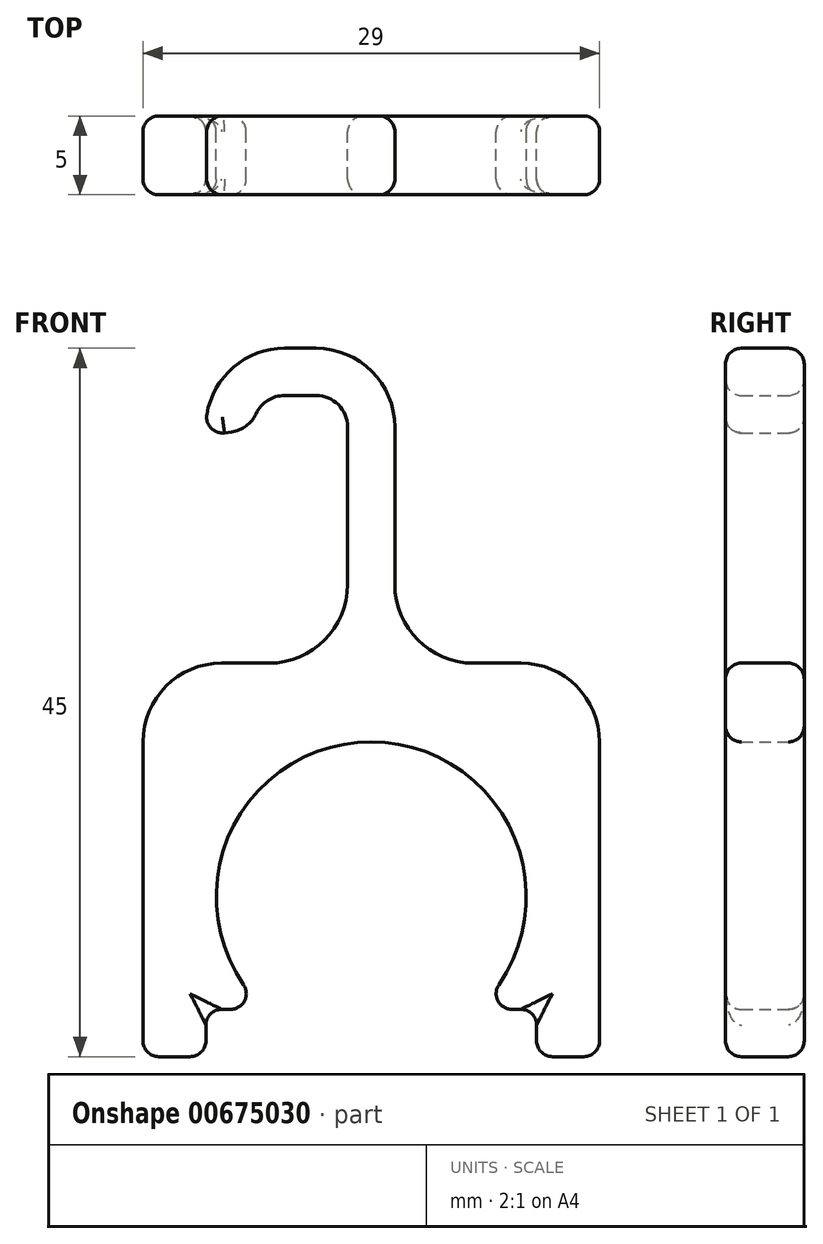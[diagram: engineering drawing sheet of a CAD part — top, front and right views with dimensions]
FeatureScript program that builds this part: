
annotation { "Feature Type Name" : "Feature", "Feature Type Description" : "" }
export const myFeature = defineFeature(function(context is Context, id is Id, definition is map)
    precondition{}
    {
        {
            var Q0;
            Q0=qCreatedBy(makeId("Front.planeOp"),FACE);
            var sketch = newSketch(context, id + "F0", { "sketchPlane" : qUnion([Q0])});
            skArc(sketch, "E0", {"start": v(6.77, -7.15) * mm, "mid": v(0, 9.85) * mm, "end": v(-6.77, -7.15) * mm});
            skLineSegment(sketch, "E1.bottom", {"start": v(-14.5, -7.15) * mm, "end": v(-6.77, -7.15) * mm});
            skLineSegment(sketch, "E2", {"start": v(14.5, -7.15) * mm, "end": v(14.5, 14.85) * mm});
            skLineSegment(sketch, "E3", {"start": v(0, 9.85) * mm, "end": v(0, 14.85) * mm, "construction": true});
            skLineSegment(sketch, "E4", {"start": v(0, 14.85) * mm, "end": v(14.5, 14.85) * mm});
            skLineSegment(sketch, "E5", {"start": v(-14.5, -7.15) * mm, "end": v(-14.5, 14.85) * mm});
            skLineSegment(sketch, "E6", {"start": v(-14.5, 14.85) * mm, "end": v(0, 14.85) * mm});
            skLineSegment(sketch, "E7.trimOffspring", {"start": v(6.77, -7.15) * mm, "end": v(14.5, -7.15) * mm});
            skLineSegment(sketch, "E8", {"start": v(6.77, -7.15) * mm, "end": v(-6.77, -7.15) * mm, "construction": true});
            skLineSegment(sketch, "E9", {"start": v(0, 0) * mm, "end": v(0, -7.15) * mm, "construction": true});
            skLineSegment(sketch, "E10", {"start": v(-1.5, 14.85) * mm, "end": v(-1.5, 29.84) * mm});
            skLineSegment(sketch, "E11", {"start": v(-1.5, 29.84) * mm, "end": v(1.5, 29.84) * mm});
            skLineSegment(sketch, "E12", {"start": v(1.5, 29.84) * mm, "end": v(1.5, 14.85) * mm});
            skArc(sketch, "E13", {"start": v(1.5, 29.84) * mm, "mid": v(0.04, 33.38) * mm, "end": v(-3.5, 34.84) * mm});
            skArc(sketch, "E14", {"start": v(-1.5, 29.84) * mm, "mid": v(-2.09, 31.26) * mm, "end": v(-3.5, 31.84) * mm});
            skLineSegment(sketch, "E15", {"start": v(-14.5, -7.15) * mm, "end": v(-14.5, -10.15) * mm});
            skLineSegment(sketch, "E16", {"start": v(-14.5, -10.15) * mm, "end": v(-10.5, -10.15) * mm});
            skLineSegment(sketch, "E17", {"start": v(-10.5, -10.15) * mm, "end": v(-10.5, -7.15) * mm});
            skLineSegment(sketch, "E18", {"start": v(14.5, -7.15) * mm, "end": v(14.5, -10.15) * mm});
            skLineSegment(sketch, "E19", {"start": v(14.5, -10.15) * mm, "end": v(10.5, -10.15) * mm});
            skLineSegment(sketch, "E20", {"start": v(10.5, -10.15) * mm, "end": v(10.5, -7.15) * mm});
            skLineSegment(sketch, "E21", {"start": v(-3.5, 29.84) * mm, "end": v(-3.5, 34.84) * mm, "construction": true});
            skPoint(sketch, "E22.orphan", {"position": v(-5.5, 29.84) * mm});
            skPoint(sketch, "E23.orphan", {"position": v(-8.5, 29.85) * mm});
            skLineSegment(sketch, "E24", {"start": v(-3.5, 31.84) * mm, "end": v(-5.5, 31.84) * mm});
            skLineSegment(sketch, "E25", {"start": v(-3.5, 34.84) * mm, "end": v(-5.5, 34.84) * mm});
            skArc(sketch, "E26", {"start": v(-5.5, 31.84) * mm, "mid": v(-6.96, 31.22) * mm, "end": v(-7.5, 29.72) * mm});
            skArc(sketch, "E27.0", {"start": v(-5.5, 34.84) * mm, "mid": v(-9.22, 33.19) * mm, "end": v(-10.47, 29.32) * mm});
            skLineSegment(sketch, "E28", {"start": v(-7.5, 29.72) * mm, "end": v(-10.47, 29.32) * mm});
            skSolve(sketch);
        }
        {
            var Q0;
            {var subQ0=sQuery(id+"F0.wireOp",EDGE,"E10");Q0=makeQuery(id+"F0.imprint","IMPRINT",FACE,{"disambiguationData":[TD([[makeQuery(id+"F0.imprint","IMPRINT",EDGE,{"derivedFrom":subQ0}),-1.0]])]});}
            var Q1;
            Q1=makeQuery(id+"F0.imprint","IMPRINT",FACE,{"disambiguationData":[TD([[makeQuery(id+"F0.imprint","IMPRINT",EDGE,{"derivedFrom":sQuery(id+"F0.wireOp",EDGE,"E11")}),1.0]])]});
            var Q2;
            Q2=makeQuery(id+"F0.imprint","IMPRINT",FACE,{"disambiguationData":[TD([[makeQuery(id+"F0.imprint","IMPRINT",EDGE,{"derivedFrom":sQuery(id+"F0.wireOp",EDGE,"E0")}),-1.0]])]});
            var Q3;
            {var subQ0=sQuery(id+"F0.wireOp",EDGE,"E15");Q3=makeQuery(id+"F0.imprint","IMPRINT",FACE,{"disambiguationData":[TD([[makeQuery(id+"F0.imprint","IMPRINT",EDGE,{"derivedFrom":subQ0}),1.0]])]});}
            var Q4;
            {var subQ0=sQuery(id+"F0.wireOp",EDGE,"E18");Q4=makeQuery(id+"F0.imprint","IMPRINT",FACE,{"disambiguationData":[TD([[makeQuery(id+"F0.imprint","IMPRINT",EDGE,{"derivedFrom":subQ0}),-1.0]])]});}
            extrude(context, id + "F1", {"entities" : qUnion([Q0, Q1, Q2, Q3, Q4]), "depth" : 5 * mm, "offsetDistance" : 25 * mm});
        }
        {
            var Q0;
            Q0=makeQuery(id+"F1.opExtrude","SWEPT_EDGE",EDGE,{"disambiguationData":[OSD([sQuery(id+"F0.wireOp",EDGE,"iK1HZVFs-EU1M-R8Xy-Kw5s-u2PyRseDFcwY"),sQuery(id+"F0.wireOp",EDGE,"iyGj0UfU-Zjkc-Cnsw-hSJO-qxqU3gxrafzM")])]});
            var Q1;
            Q1=makeQuery(id+"F1.opExtrude","SWEPT_EDGE",EDGE,{"disambiguationData":[OSD([sQuery(id+"F0.wireOp",EDGE,"E14"),sQuery(id+"F0.wireOp",EDGE,"iyGj0UfU-Zjkc-Cnsw-hSJO-qxqU3gxrafzM")])]});
            var Q2;
            Q2=makeQuery(id+"F1.opExtrude","SWEPT_EDGE",EDGE,{"disambiguationData":[OSD([sQuery(id+"F0.wireOp",EDGE,"E0"),sQuery(id+"F0.wireOp",EDGE,"E1.bottom")])]});
            var Q3;
            Q3=makeQuery(id+"F1.opExtrude","SWEPT_EDGE",EDGE,{"disambiguationData":[OSD([sQuery(id+"F0.wireOp",EDGE,"E0"),sQuery(id+"F0.wireOp",EDGE,"E7.trimOffspring")])]});
            fillet(context, id + "F2", {"entities" : qUnion([Q0, Q1, Q2, Q3]), "radius" : 1 * mm, "tangentPropagation" : true, "allowEdgeOverflow" : false});
        }
        {
            var Q0;
            Q0=makeQuery(id+"F1.opExtrude","SWEPT_EDGE",EDGE,{"disambiguationData":[OSD([sQuery(id+"F0.wireOp",EDGE,"E5"),sQuery(id+"F0.wireOp",EDGE,"E6")])]});
            var Q1;
            Q1=makeQuery(id+"F1.opExtrude","SWEPT_EDGE",EDGE,{"disambiguationData":[OSD([sQuery(id+"F0.wireOp",EDGE,"E6"),sQuery(id+"F0.wireOp",EDGE,"E10")])]});
            var Q2;
            Q2=makeQuery(id+"F1.opExtrude","SWEPT_EDGE",EDGE,{"disambiguationData":[OSD([sQuery(id+"F0.wireOp",EDGE,"E4"),sQuery(id+"F0.wireOp",EDGE,"E12")])]});
            var Q3;
            Q3=makeQuery(id+"F1.opExtrude","SWEPT_EDGE",EDGE,{"disambiguationData":[OSD([sQuery(id+"F0.wireOp",EDGE,"E2"),sQuery(id+"F0.wireOp",EDGE,"E4")])]});
            fillet(context, id + "F3", {"entities" : qUnion([Q0, Q1, Q2, Q3]), "radius" : 5 * mm, "tangentPropagation" : true, "allowEdgeOverflow" : false});
        }
        {
            var Q0;
            Q0=makeQuery(id+"F1.opExtrude","CAP_FACE",FACE,{"disambiguationData":[OSD([sQuery(id+"F0.wireOp",EDGE,"E0"),sQuery(id+"F0.wireOp",EDGE,"E1.bottom"),sQuery(id+"F0.wireOp",EDGE,"E2"),sQuery(id+"F0.wireOp",EDGE,"E4"),sQuery(id+"F0.wireOp",EDGE,"E5"),sQuery(id+"F0.wireOp",EDGE,"E6"),sQuery(id+"F0.wireOp",EDGE,"E7.trimOffspring"),sQuery(id+"F0.wireOp",EDGE,"E10"),sQuery(id+"F0.wireOp",EDGE,"E12"),sQuery(id+"F0.wireOp",EDGE,"E13"),sQuery(id+"F0.wireOp",EDGE,"E14"),sQuery(id+"F0.wireOp",EDGE,"iK1HZVFs-EU1M-R8Xy-Kw5s-u2PyRseDFcwY"),sQuery(id+"F0.wireOp",EDGE,"iyGj0UfU-Zjkc-Cnsw-hSJO-qxqU3gxrafzM")])],"isStart":false});
            var Q1;
            Q1=makeQuery(id+"F1.opExtrude","CAP_FACE",FACE,{"disambiguationData":[OSD([sQuery(id+"F0.wireOp",EDGE,"E0"),sQuery(id+"F0.wireOp",EDGE,"E1.bottom"),sQuery(id+"F0.wireOp",EDGE,"E2"),sQuery(id+"F0.wireOp",EDGE,"E4"),sQuery(id+"F0.wireOp",EDGE,"E5"),sQuery(id+"F0.wireOp",EDGE,"E6"),sQuery(id+"F0.wireOp",EDGE,"E7.trimOffspring"),sQuery(id+"F0.wireOp",EDGE,"E10"),sQuery(id+"F0.wireOp",EDGE,"E12"),sQuery(id+"F0.wireOp",EDGE,"E13"),sQuery(id+"F0.wireOp",EDGE,"E14"),sQuery(id+"F0.wireOp",EDGE,"iK1HZVFs-EU1M-R8Xy-Kw5s-u2PyRseDFcwY"),sQuery(id+"F0.wireOp",EDGE,"iyGj0UfU-Zjkc-Cnsw-hSJO-qxqU3gxrafzM")])],"isStart":true});
            fillet(context, id + "F4", {"entities" : qUnion([Q0, Q1]), "radius" : 1 * mm, "tangentPropagation" : true, "allowEdgeOverflow" : false});
        }
        {
            var Q0;
            Q0=makeQuery(id+"F1.opExtrude","SWEPT_EDGE",EDGE,{"disambiguationData":[OSD([sQuery(id+"F0.wireOp",EDGE,"E15"),sQuery(id+"F0.wireOp",EDGE,"E16")])]});
            var Q1;
            Q1=makeQuery(id+"F1.opExtrude","SWEPT_EDGE",EDGE,{"disambiguationData":[OSD([sQuery(id+"F0.wireOp",EDGE,"E16"),sQuery(id+"F0.wireOp",EDGE,"E17")])]});
            var Q2;
            Q2=makeQuery(id+"F1.opExtrude","SWEPT_EDGE",EDGE,{"disambiguationData":[OSD([sQuery(id+"F0.wireOp",EDGE,"E19"),sQuery(id+"F0.wireOp",EDGE,"E20")])]});
            var Q3;
            Q3=makeQuery(id+"F1.opExtrude","SWEPT_EDGE",EDGE,{"disambiguationData":[OSD([sQuery(id+"F0.wireOp",EDGE,"E18"),sQuery(id+"F0.wireOp",EDGE,"E19")])]});
            var Q4;
            Q4=makeQuery(id+"F1.opExtrude","SWEPT_EDGE",EDGE,{"disambiguationData":[OSD([sQuery(id+"F0.wireOp",EDGE,"E1.bottom"),sQuery(id+"F0.wireOp",EDGE,"E17")])]});
            var Q5;
            Q5=makeQuery(id+"F1.opExtrude","SWEPT_EDGE",EDGE,{"disambiguationData":[OSD([sQuery(id+"F0.wireOp",EDGE,"E7.trimOffspring"),sQuery(id+"F0.wireOp",EDGE,"E20")])]});
            fillet(context, id + "F5", {"entities" : qUnion([Q0, Q1, Q2, Q3, Q4, Q5]), "radius" : 1 * mm, "tangentPropagation" : true, "allowEdgeOverflow" : false});
        }
        {
            var Q0;
            Q0=makeQuery(id+"F1.opExtrude","SWEPT_EDGE",EDGE,{"disambiguationData":[OSD([sQuery(id+"F0.wireOp",EDGE,"E27.0"),sQuery(id+"F0.wireOp",EDGE,"E28")])]});
            fillet(context, id + "F6", {"entities" : qUnion([Q0]), "radius" : 1 * mm, "tangentPropagation" : true, "allowEdgeOverflow" : false});
        }
        {
            var Q0;
            Q0=makeQuery(id+"F1.opExtrude","SWEPT_EDGE",EDGE,{"disambiguationData":[OSD([sQuery(id+"F0.wireOp",EDGE,"E26"),sQuery(id+"F0.wireOp",EDGE,"E28")])]});
            fillet(context, id + "F7", {"entities" : qUnion([Q0]), "radius" : 2 * mm, "tangentPropagation" : true, "allowEdgeOverflow" : false});
        }
    });
